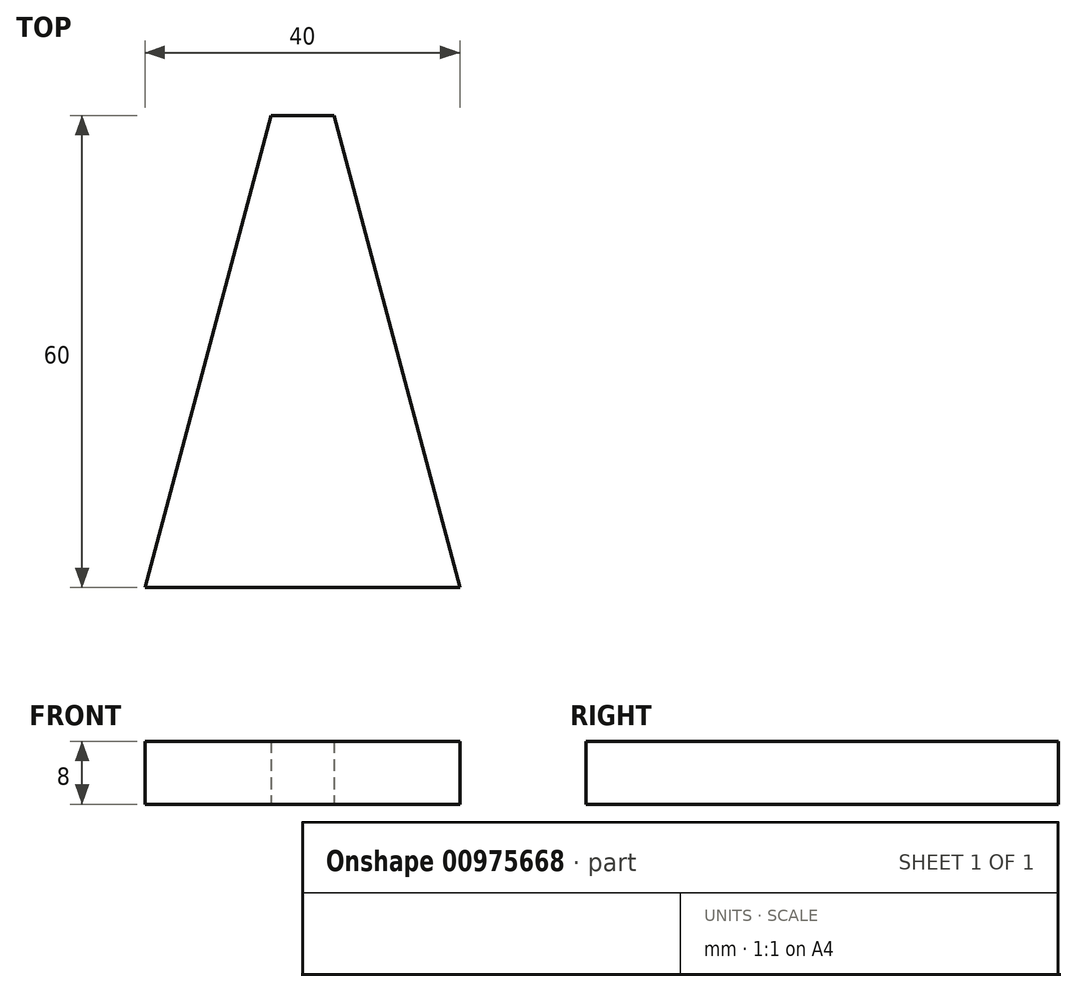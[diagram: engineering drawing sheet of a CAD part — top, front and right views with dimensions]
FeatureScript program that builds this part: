
annotation { "Feature Type Name" : "Feature", "Feature Type Description" : "" }
export const myFeature = defineFeature(function(context is Context, id is Id, definition is map)
    precondition{}
    {
        {
            var Q0;
            Q0=qCreatedBy(makeId("Top.planeOp"),FACE);
            var sketch = newSketch(context, id + "F0", { "sketchPlane" : qUnion([Q0])});
            skLineSegment(sketch, "E0", {"start": v(-25.59, 39.8) * mm, "end": v(-21.59, 39.8) * mm});
            skLineSegment(sketch, "E1", {"start": v(-21.59, -20.2) * mm, "end": v(-41.59, -20.2) * mm});
            skLineSegment(sketch, "E2", {"start": v(-41.59, -20.2) * mm, "end": v(-25.59, 39.8) * mm});
            skLineSegment(sketch, "E3.MirrorCS", {"start": v(-1.59, -20.2) * mm, "end": v(-17.59, 39.8) * mm});
            skLineSegment(sketch, "E4.MirrorCS", {"start": v(-21.59, -20.2) * mm, "end": v(-1.59, -20.2) * mm});
            skLineSegment(sketch, "E5.MirrorCS", {"start": v(-17.59, 39.8) * mm, "end": v(-21.59, 39.8) * mm});
            skSolve(sketch);
        }
        {
            var Q0;
            Q0=makeQuery(id+"F0.imprint","IMPRINT",FACE,{"disambiguationData":[TD([[makeQuery(id+"F0.imprint","IMPRINT",EDGE,{"derivedFrom":sQuery(id+"F0.wireOp",EDGE,"E0")}),-1.0]])]});
            extrude(context, id + "F1", {"entities" : qUnion([Q0]), "depth" : 8 * mm, "offsetDistance" : 25 * mm});
        }
    });
